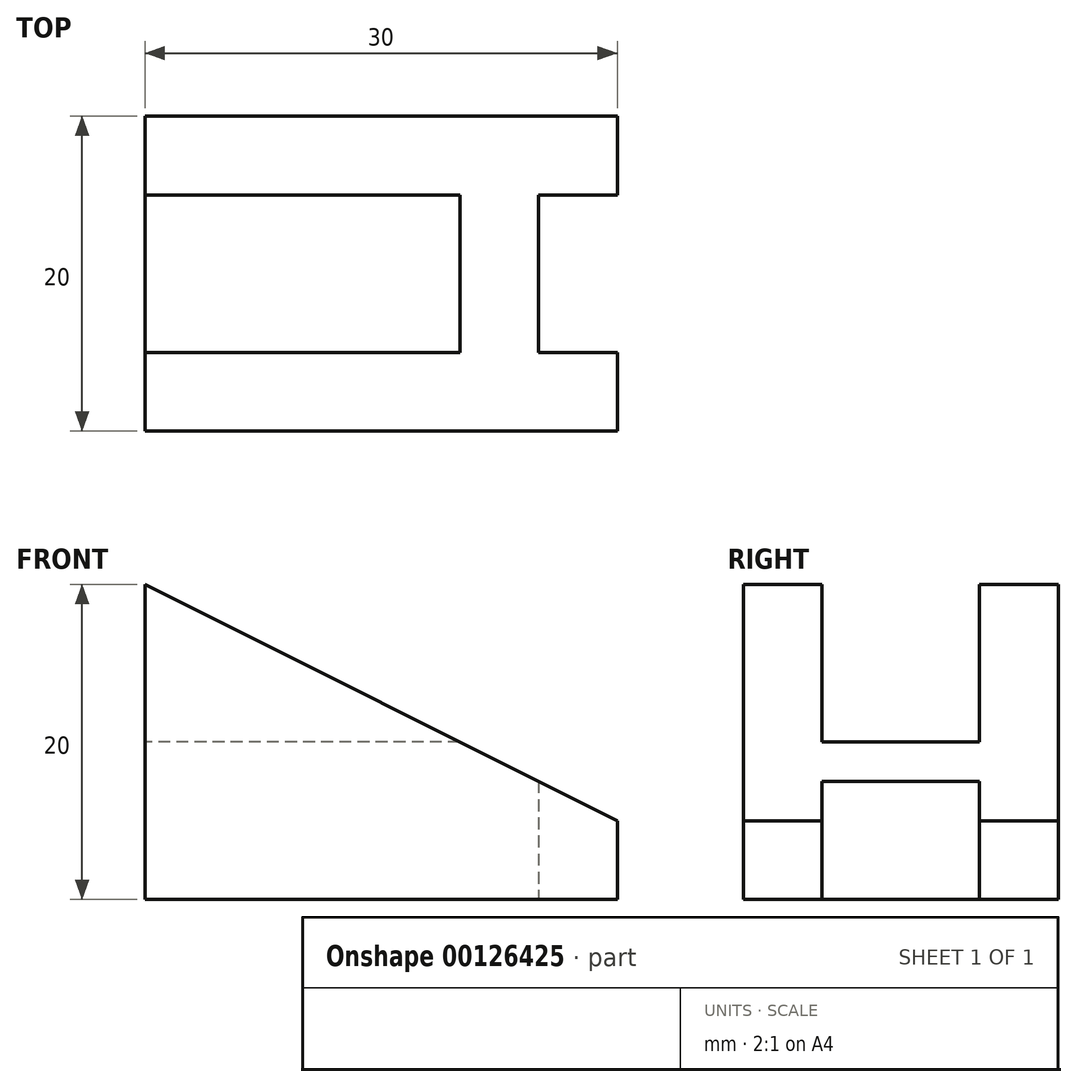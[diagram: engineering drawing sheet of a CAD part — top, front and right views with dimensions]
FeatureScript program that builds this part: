
annotation { "Feature Type Name" : "Feature", "Feature Type Description" : "" }
export const myFeature = defineFeature(function(context is Context, id is Id, definition is map)
    precondition{}
    {
        {
            var Q0;
            Q0=qCreatedBy(makeId("Front.planeOp"),FACE);
            var sketch = newSketch(context, id + "F0", { "sketchPlane" : qUnion([Q0])});
            skLineSegment(sketch, "E0", {"start": v(0, 0) * mm, "end": v(-30, 0) * mm});
            skLineSegment(sketch, "E1", {"start": v(-30, 0) * mm, "end": v(-30, 20) * mm});
            skLineSegment(sketch, "E2", {"start": v(0, 0) * mm, "end": v(0, 5) * mm});
            skLineSegment(sketch, "E3", {"start": v(0, 5) * mm, "end": v(-30, 20) * mm});
            skSolve(sketch);
        }
        {
            var Q0;
            Q0 = qSketchRegion(id + "F0", true);
            extrude(context, id + "F1", {"entities" : qUnion([Q0]), "endBound" : BoundingType.SYMMETRIC, "oppositeDirection" : true, "depth" : 20 * mm});
        }
        {
            var Q0;
            Q0=makeQuery(id+"F1.opExtrude","SWEPT_FACE",FACE,{"disambiguationData":[OSD([sQuery(id+"F0.wireOp",EDGE,"E1")])]});
            var sketch = newSketch(context, id + "F2", { "sketchPlane" : qUnion([Q0])});
            skLineSegment(sketch, "E4", {"start": v(-10, 20) * mm, "end": v(-5, 20) * mm});
            skLineSegment(sketch, "E5", {"start": v(-5, 20) * mm, "end": v(-5, 10) * mm});
            skLineSegment(sketch, "E6", {"start": v(-5, 10) * mm, "end": v(5, 10) * mm});
            skLineSegment(sketch, "E7", {"start": v(5, 10) * mm, "end": v(5, 20) * mm});
            skLineSegment(sketch, "E8", {"start": v(5, 20) * mm, "end": v(10, 20) * mm});
            skLineSegment(sketch, "E9", {"start": v(-5, 20) * mm, "end": v(5, 20) * mm});
            skSolve(sketch);
        }
        {
            var Q0;
            Q0 = qSketchRegion(id + "F2", true);
            extrude(context, id + "F3", {"entities" : qUnion([Q0]), "operationType" : NewBodyOperationType.REMOVE, "oppositeDirection" : true, "depth" : 20 * mm});
        }
        {
            var Q0;
            Q0=makeQuery(id+"F1.opExtrude","SWEPT_FACE",FACE,{"disambiguationData":[OSD([sQuery(id+"F0.wireOp",EDGE,"E0")])]});
            var sketch = newSketch(context, id + "F4", { "sketchPlane" : qUnion([Q0])});
            skLineSegment(sketch, "E10", {"start": v(0, 10) * mm, "end": v(0, 5) * mm});
            skLineSegment(sketch, "E11", {"start": v(0, 5) * mm, "end": v(-5, 5) * mm});
            skLineSegment(sketch, "E12", {"start": v(-5, 5) * mm, "end": v(-5, -5) * mm});
            skLineSegment(sketch, "E13", {"start": v(-5, -5) * mm, "end": v(0, -5) * mm});
            skLineSegment(sketch, "E14", {"start": v(0, -5) * mm, "end": v(0, -10) * mm});
            skLineSegment(sketch, "E15", {"start": v(0, 5) * mm, "end": v(0, -5) * mm});
            skSolve(sketch);
        }
        {
            var Q0;
            Q0 = qSketchRegion(id + "F4", true);
            extrude(context, id + "F5", {"entities" : qUnion([Q0]), "operationType" : NewBodyOperationType.REMOVE, "oppositeDirection" : true, "depth" : 25 * mm});
        }
    });
